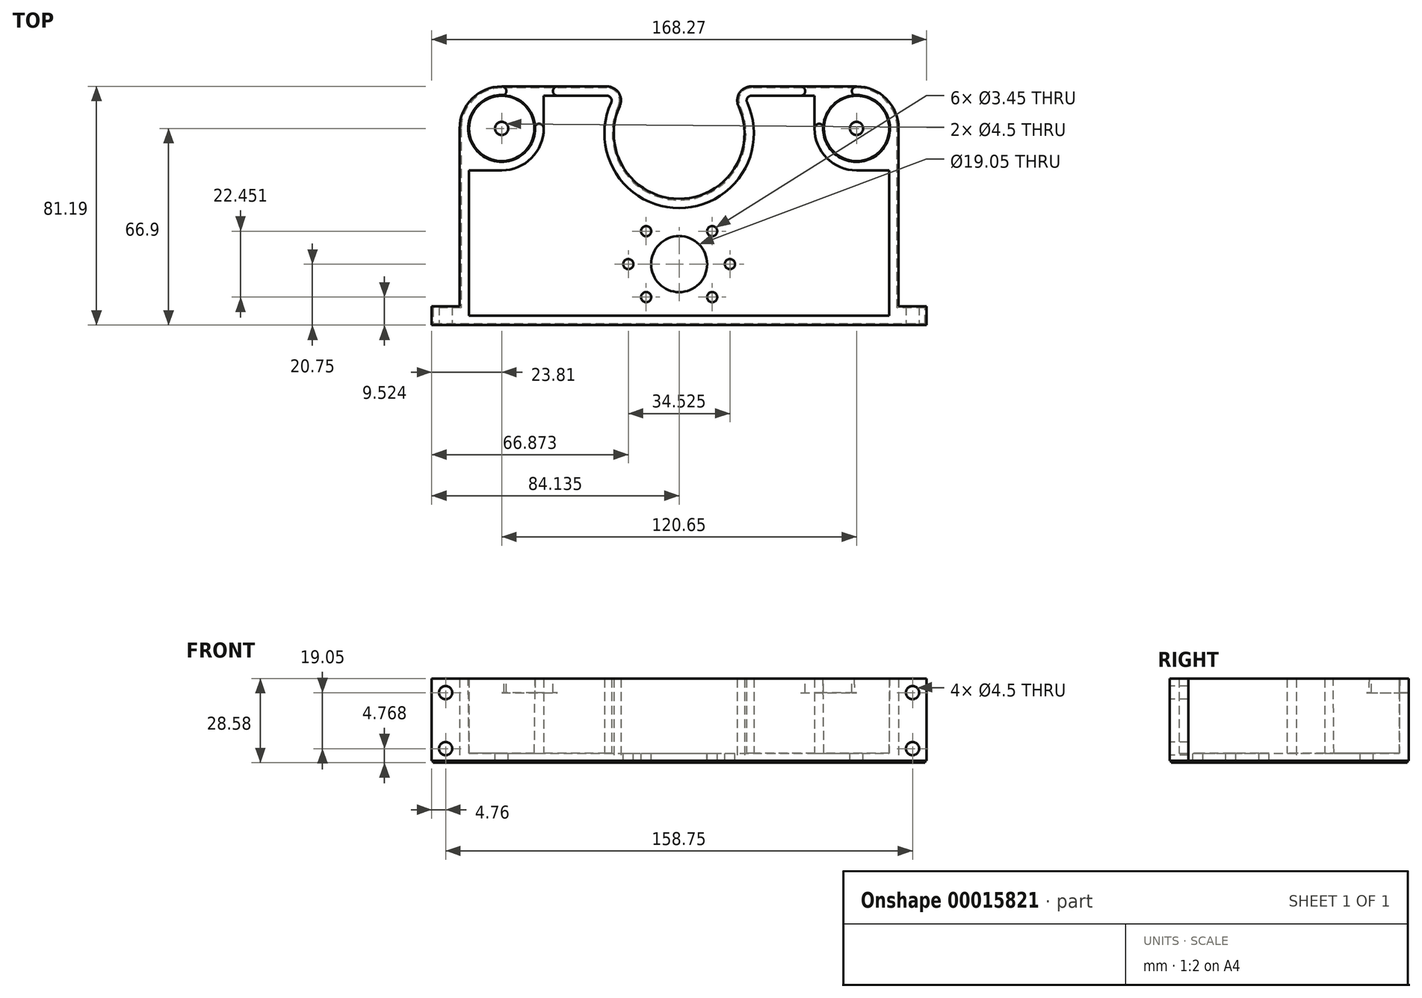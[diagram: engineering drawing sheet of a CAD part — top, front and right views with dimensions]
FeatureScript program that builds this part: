
annotation { "Feature Type Name" : "Feature", "Feature Type Description" : "" }
export const myFeature = defineFeature(function(context is Context, id is Id, definition is map)
    precondition{}
    {
        {
            var Q0;
            Q0=qCreatedBy(makeId("Top.planeOp"),FACE);
            var sketch = newSketch(context, id + "F0", { "sketchPlane" : qUnion([Q0])});
            skCircle(sketch, "E0", {"center": v(0, 0) * mm, "radius": 11.11 * mm});
            skLineSegment(sketch, "E1", {"start": v(0, 0) * mm, "end": v(120.65, 0) * mm, "construction": true});
            skCircle(sketch, "E2", {"center": v(120.65, 0) * mm, "radius": 11.11 * mm});
            skArc(sketch, "E3", {"start": v(0, 14.29) * mm, "mid": v(-10.1, 10.1) * mm, "end": v(-14.29, 0) * mm});
            skArc(sketch, "E4", {"start": v(134.94, 0) * mm, "mid": v(130.75, 10.1) * mm, "end": v(120.65, 14.29) * mm});
            skLineSegment(sketch, "E5", {"start": v(-14.29, 0) * mm, "end": v(-14.29, -60.55) * mm});
            skLineSegment(sketch, "E6", {"start": v(134.94, 0) * mm, "end": v(134.94, -60.55) * mm});
            skLineSegment(sketch, "E7", {"start": v(134.94, -60.55) * mm, "end": v(144.46, -60.55) * mm});
            skLineSegment(sketch, "E8", {"start": v(144.46, -60.55) * mm, "end": v(144.46, -66.9) * mm});
            skLineSegment(sketch, "E9", {"start": v(144.46, -66.9) * mm, "end": v(-23.81, -66.9) * mm});
            skLineSegment(sketch, "E10", {"start": v(-23.81, -66.9) * mm, "end": v(-23.81, -60.55) * mm});
            skLineSegment(sketch, "E11", {"start": v(-23.81, -60.55) * mm, "end": v(-14.29, -60.55) * mm});
            skLineSegment(sketch, "E12", {"start": v(84.87, 14.29) * mm, "end": v(35.78, 14.29) * mm, "construction": true});
            skArc(sketch, "E13", {"start": v(40.11, 7.54) * mm, "mid": v(60.32, -23.93) * mm, "end": v(80.54, 7.54) * mm});
            skLineSegment(sketch, "E14", {"start": v(60.33, -1.7) * mm, "end": v(60.33, 0) * mm, "construction": true});
            skArc(sketch, "E15", {"start": v(40.11, 7.54) * mm, "mid": v(39.8, 12.1) * mm, "end": v(35.78, 14.29) * mm});
            skLineSegment(sketch, "E16", {"start": v(0, 14.29) * mm, "end": v(35.78, 14.29) * mm});
            skArc(sketch, "E17", {"start": v(84.87, 14.29) * mm, "mid": v(80.86, 12.1) * mm, "end": v(80.54, 7.54) * mm});
            skLineSegment(sketch, "E18", {"start": v(84.87, 14.29) * mm, "end": v(120.65, 14.29) * mm});
            skLineSegment(sketch, "E19", {"start": v(60.33, -1.7) * mm, "end": v(60.33, -23.93) * mm, "construction": true});
            skLineSegment(sketch, "E20", {"start": v(60.33, -23.93) * mm, "end": v(60.33, -66.9) * mm, "construction": true});
            skSolve(sketch);
        }
        {
            var Q0;
            Q0 = qSketchRegion(id + "F0", true);
            extrude(context, id + "F1", {"entities" : qUnion([Q0]), "depth" : 25.4 * mm});
        }
        {
            var Q0;
            Q0=makeQuery(id+"F1.opExtrude","CAP_FACE",FACE,{"disambiguationData":[OSD([sQuery(id+"F0.wireOp",EDGE,"E0"),sQuery(id+"F0.wireOp",EDGE,"E2"),sQuery(id+"F0.wireOp",EDGE,"vQT7KybJ-lzgk-kh55-kQ7M-RuszsokMCCUL"),sQuery(id+"F0.wireOp",EDGE,"E3"),sQuery(id+"F0.wireOp",EDGE,"E4"),sQuery(id+"F0.wireOp",EDGE,"E5"),sQuery(id+"F0.wireOp",EDGE,"E6"),sQuery(id+"F0.wireOp",EDGE,"E7"),sQuery(id+"F0.wireOp",EDGE,"E8"),sQuery(id+"F0.wireOp",EDGE,"E9"),sQuery(id+"F0.wireOp",EDGE,"E10"),sQuery(id+"F0.wireOp",EDGE,"E11")])],"isStart":false});
            shell(context, id + "F2", {"entities" : qUnion([Q0]), "thickness" : 3.17 * mm});
        }
        {
            var Q0;
            Q0=makeQuery(id+"F2.opShell","OFFSET_FACE",FACE,{"disambiguationData":[OSD([sQuery(id+"F0.wireOp",EDGE,"E0"),sQuery(id+"F0.wireOp",EDGE,"E2"),sQuery(id+"F0.wireOp",EDGE,"vQT7KybJ-lzgk-kh55-kQ7M-RuszsokMCCUL"),sQuery(id+"F0.wireOp",EDGE,"E3"),sQuery(id+"F0.wireOp",EDGE,"E4"),sQuery(id+"F0.wireOp",EDGE,"E5"),sQuery(id+"F0.wireOp",EDGE,"E6"),sQuery(id+"F0.wireOp",EDGE,"E7"),sQuery(id+"F0.wireOp",EDGE,"E8"),sQuery(id+"F0.wireOp",EDGE,"E9"),sQuery(id+"F0.wireOp",EDGE,"E10"),sQuery(id+"F0.wireOp",EDGE,"E11")])]});
            var sketch = newSketch(context, id + "F3", { "sketchPlane" : qUnion([Q0])});
            skArc(sketch, "E21", {"start": v(14.29, 0) * mm, "mid": v(12.9, 6.16) * mm, "end": v(8.98, 11.11) * mm});
            skArc(sketch, "E22", {"start": v(-11.11, -8.98) * mm, "mid": v(-6.16, -12.9) * mm, "end": v(0, -14.29) * mm});
            skLineSegment(sketch, "E23.bottom", {"start": v(-11.11, -8.98) * mm, "end": v(0, -8.98) * mm, "construction": true});
            skLineSegment(sketch, "E23.top", {"start": v(-11.11, -14.29) * mm, "end": v(0, -14.29) * mm});
            skLineSegment(sketch, "E23.left", {"start": v(-11.11, -8.98) * mm, "end": v(-11.11, -14.29) * mm});
            skLineSegment(sketch, "E23.right", {"start": v(0, -8.98) * mm, "end": v(0, -14.29) * mm, "construction": true});
            skLineSegment(sketch, "E24.bottom", {"start": v(14.29, 0) * mm, "end": v(8.98, 0) * mm, "construction": true});
            skLineSegment(sketch, "E24.top", {"start": v(14.29, 11.11) * mm, "end": v(8.98, 11.11) * mm});
            skLineSegment(sketch, "E24.left", {"start": v(14.29, 0) * mm, "end": v(14.29, 11.11) * mm});
            skLineSegment(sketch, "E24.right", {"start": v(8.98, 0) * mm, "end": v(8.98, 11.11) * mm, "construction": true});
            skArc(sketch, "E25", {"start": v(111.67, 11.11) * mm, "mid": v(107.76, 6.16) * mm, "end": v(106.36, 0) * mm});
            skArc(sketch, "E26", {"start": v(120.65, -14.29) * mm, "mid": v(126.8, -12.9) * mm, "end": v(131.76, -8.98) * mm});
            skLineSegment(sketch, "E27.bottom", {"start": v(106.36, 0) * mm, "end": v(111.67, 0) * mm, "construction": true});
            skLineSegment(sketch, "E27.top", {"start": v(106.36, 11.11) * mm, "end": v(111.67, 11.11) * mm});
            skLineSegment(sketch, "E27.left", {"start": v(106.36, 0) * mm, "end": v(106.36, 11.11) * mm});
            skLineSegment(sketch, "E27.right", {"start": v(111.67, 0) * mm, "end": v(111.67, 11.11) * mm, "construction": true});
            skLineSegment(sketch, "E28.bottom", {"start": v(120.65, -14.29) * mm, "end": v(131.76, -14.29) * mm});
            skLineSegment(sketch, "E28.top", {"start": v(120.65, -8.98) * mm, "end": v(131.76, -8.98) * mm, "construction": true});
            skLineSegment(sketch, "E28.left", {"start": v(120.65, -14.29) * mm, "end": v(120.65, -8.98) * mm, "construction": true});
            skLineSegment(sketch, "E28.right", {"start": v(131.76, -14.29) * mm, "end": v(131.76, -8.98) * mm});
            skSolve(sketch);
        }
        {
            var Q0;
            Q0 = qSketchRegion(id + "F3", true);
            var Q1;
            Q1=makeQuery(id+"F1.opExtrude","CAP_FACE",FACE,{"disambiguationData":[OSD([sQuery(id+"F0.wireOp",EDGE,"E0"),sQuery(id+"F0.wireOp",EDGE,"E2"),sQuery(id+"F0.wireOp",EDGE,"vQT7KybJ-lzgk-kh55-kQ7M-RuszsokMCCUL"),sQuery(id+"F0.wireOp",EDGE,"E3"),sQuery(id+"F0.wireOp",EDGE,"E4"),sQuery(id+"F0.wireOp",EDGE,"E5"),sQuery(id+"F0.wireOp",EDGE,"E6"),sQuery(id+"F0.wireOp",EDGE,"E7"),sQuery(id+"F0.wireOp",EDGE,"E8"),sQuery(id+"F0.wireOp",EDGE,"E9"),sQuery(id+"F0.wireOp",EDGE,"E10"),sQuery(id+"F0.wireOp",EDGE,"E11")])],"isStart":false});
            extrude(context, id + "F4", {"entities" : qUnion([Q0]), "operationType" : NewBodyOperationType.ADD, "endBound" : BoundingType.UP_TO_SURFACE, "endBoundEntityFace" : qUnion([Q1]), "depth" : 25.4 * mm});
        }
        {
            var Q0;
            Q0=makeQuery(id+"F2.opShell","OFFSET_FACE",FACE,{"disambiguationData":[OSD([sQuery(id+"F0.wireOp",EDGE,"E0"),sQuery(id+"F0.wireOp",EDGE,"E2"),sQuery(id+"F0.wireOp",EDGE,"vQT7KybJ-lzgk-kh55-kQ7M-RuszsokMCCUL"),sQuery(id+"F0.wireOp",EDGE,"E3"),sQuery(id+"F0.wireOp",EDGE,"E4"),sQuery(id+"F0.wireOp",EDGE,"E5"),sQuery(id+"F0.wireOp",EDGE,"E6"),sQuery(id+"F0.wireOp",EDGE,"E7"),sQuery(id+"F0.wireOp",EDGE,"E8"),sQuery(id+"F0.wireOp",EDGE,"E9"),sQuery(id+"F0.wireOp",EDGE,"E10"),sQuery(id+"F0.wireOp",EDGE,"E11")])]});
            var Q1;
            Q1=makeQuery(id+"F1.opExtrude","CAP_FACE",FACE,{"disambiguationData":[OSD([sQuery(id+"F0.wireOp",EDGE,"E0"),sQuery(id+"F0.wireOp",EDGE,"E2"),sQuery(id+"F0.wireOp",EDGE,"vQT7KybJ-lzgk-kh55-kQ7M-RuszsokMCCUL"),sQuery(id+"F0.wireOp",EDGE,"E3"),sQuery(id+"F0.wireOp",EDGE,"E4"),sQuery(id+"F0.wireOp",EDGE,"E5"),sQuery(id+"F0.wireOp",EDGE,"E6"),sQuery(id+"F0.wireOp",EDGE,"E7"),sQuery(id+"F0.wireOp",EDGE,"E8"),sQuery(id+"F0.wireOp",EDGE,"E9"),sQuery(id+"F0.wireOp",EDGE,"E10"),sQuery(id+"F0.wireOp",EDGE,"E11")])],"isStart":true});
            extrude(context, id + "F5", {"entities" : qUnion([Q0]), "operationType" : NewBodyOperationType.REMOVE, "endBound" : BoundingType.UP_TO_SURFACE, "oppositeDirection" : true, "endBoundEntityFace" : qUnion([Q1]), "depth" : 25.4 * mm});
        }
        {
            var Q0;
            Q0=makeQuery(id+"F1.opExtrude","CAP_FACE",FACE,{"disambiguationData":[OSD([sQuery(id+"F0.wireOp",EDGE,"E0"),sQuery(id+"F0.wireOp",EDGE,"E2"),sQuery(id+"F0.wireOp",EDGE,"vQT7KybJ-lzgk-kh55-kQ7M-RuszsokMCCUL"),sQuery(id+"F0.wireOp",EDGE,"E3"),sQuery(id+"F0.wireOp",EDGE,"E4"),sQuery(id+"F0.wireOp",EDGE,"E5"),sQuery(id+"F0.wireOp",EDGE,"E6"),sQuery(id+"F0.wireOp",EDGE,"E7"),sQuery(id+"F0.wireOp",EDGE,"E8"),sQuery(id+"F0.wireOp",EDGE,"E9"),sQuery(id+"F0.wireOp",EDGE,"E10"),sQuery(id+"F0.wireOp",EDGE,"E11")])],"isStart":true});
            var sketch = newSketch(context, id + "F6", { "sketchPlane" : qUnion([Q0])});
            skCircle(sketch, "E29", {"center": v(120.65, 0) * mm, "radius": 2.25 * mm});
            skCircle(sketch, "E30", {"center": v(0, 0) * mm, "radius": 2.25 * mm});
            skLineSegment(sketch, "E31", {"start": v(120.65, 0) * mm, "end": v(0, 0) * mm, "construction": true});
            skLineSegment(sketch, "E32.bottom", {"start": v(49.1, 34.92) * mm, "end": v(71.55, 34.92) * mm, "construction": true});
            skLineSegment(sketch, "E32.top", {"start": v(49.1, 57.38) * mm, "end": v(71.55, 57.38) * mm, "construction": true});
            skLineSegment(sketch, "E32.left", {"start": v(49.1, 34.92) * mm, "end": v(49.1, 57.38) * mm, "construction": true});
            skLineSegment(sketch, "E32.right", {"start": v(71.55, 34.92) * mm, "end": v(71.55, 57.38) * mm, "construction": true});
            skPoint(sketch, "E32.middle", {"position": v(60.33, 46.15) * mm});
            skCircle(sketch, "E33", {"center": v(60.33, 46.15) * mm, "radius": 11.11 * mm, "construction": true});
            skCircle(sketch, "E34", {"center": v(49.1, 34.92) * mm, "radius": 4.76 * mm, "construction": true});
            skCircle(sketch, "E35", {"center": v(71.55, 34.92) * mm, "radius": 1.73 * mm});
            skCircle(sketch, "E36", {"center": v(49.1, 34.92) * mm, "radius": 1.73 * mm});
            skCircle(sketch, "E37", {"center": v(49.1, 57.38) * mm, "radius": 1.73 * mm});
            skCircle(sketch, "E38", {"center": v(71.55, 57.38) * mm, "radius": 1.73 * mm});
            skCircle(sketch, "E39", {"center": v(60.33, 46.15) * mm, "radius": 9.53 * mm});
            skLineSegment(sketch, "E40", {"start": v(60.32, 46.15) * mm, "end": v(60.33, 0) * mm, "construction": true});
            skLineSegment(sketch, "E41", {"start": v(77.59, 46.15) * mm, "end": v(43.06, 46.15) * mm, "construction": true});
            skCircle(sketch, "E42", {"center": v(77.59, 46.15) * mm, "radius": 1.73 * mm});
            skCircle(sketch, "E43", {"center": v(43.06, 46.15) * mm, "radius": 1.73 * mm});
            skSolve(sketch);
        }
        {
            var Q0;
            {var subQ13=sQuery(id+"F0.wireOp",EDGE,"E0");var subQ16=makeQuery(id+"F1.opExtrude","CAP_EDGE",EDGE,{"disambiguationData":[OSD([subQ13])],"isStart":true});Q0=makeQuery(id+"F6.imprint","IMPRINT",FACE,{"disambiguationData":[TD([[makeQuery(id+"F6.imprint","IMPRINT",EDGE,{"derivedFrom":subQ16}),1.0]])]});}
            var Q1;
            Q1=makeQuery(id+"F6.imprint","IMPRINT",FACE,{"disambiguationData":[TD([[makeQuery(id+"F6.imprint","IMPRINT",EDGE,{"derivedFrom":sQuery(id+"F6.wireOp",EDGE,"E35")}),-1.0]])]});
            var Q2;
            Q2=makeQuery(id+"F6.imprint","IMPRINT",FACE,{"disambiguationData":[TD([[makeQuery(id+"F6.imprint","IMPRINT",EDGE,{"derivedFrom":sQuery(id+"F6.wireOp",EDGE,"E30")}),-1.0]])]});
            var Q3;
            Q3=makeQuery(id+"F6.imprint","IMPRINT",FACE,{"disambiguationData":[TD([[makeQuery(id+"F6.imprint","IMPRINT",EDGE,{"derivedFrom":sQuery(id+"F6.wireOp",EDGE,"E29")}),-1.0]])]});
            extrude(context, id + "F7", {"entities" : qUnion([Q0, Q1, Q2, Q3]), "operationType" : NewBodyOperationType.ADD, "depth" : 3.17 * mm});
        }
        {
            var Q0;
            {var subQ0=sQuery(id+"F0.wireOp",EDGE,"E9");Q0=makeQuery(id+"F7.boolean.opBoolean","MERGE",FACE,{"derivedFrom":[makeQuery(id+"F1.opExtrude","SWEPT_FACE",FACE,{"disambiguationData":[OSD([subQ0])]}),makeQuery(id+"F7.opExtrude","SWEPT_FACE",FACE,{"disambiguationData":[OSD([subQ0])]})]});}
            var sketch = newSketch(context, id + "F8", { "sketchPlane" : qUnion([Q0])});
            skLineSegment(sketch, "E44.bottom", {"start": v(-19.05, 25.4) * mm, "end": v(-23.81, 25.4) * mm, "construction": true});
            skLineSegment(sketch, "E44.top", {"start": v(-19.05, 20.64) * mm, "end": v(-23.81, 20.64) * mm, "construction": true});
            skLineSegment(sketch, "E44.left", {"start": v(-19.05, 25.4) * mm, "end": v(-19.05, 20.64) * mm, "construction": true});
            skLineSegment(sketch, "E44.right", {"start": v(-23.81, 25.4) * mm, "end": v(-23.81, 20.64) * mm, "construction": true});
            skLineSegment(sketch, "E45", {"start": v(60.33, 25.4) * mm, "end": v(60.33, -3.18) * mm, "construction": true});
            skLineSegment(sketch, "E46.bottom", {"start": v(-19.05, 20.64) * mm, "end": v(139.7, 20.64) * mm, "construction": true});
            skLineSegment(sketch, "E46.top", {"start": v(-19.05, 1.59) * mm, "end": v(139.7, 1.59) * mm, "construction": true});
            skLineSegment(sketch, "E46.left", {"start": v(-19.05, 20.64) * mm, "end": v(-19.05, 1.59) * mm, "construction": true});
            skLineSegment(sketch, "E46.right", {"start": v(139.7, 20.64) * mm, "end": v(139.7, 1.59) * mm, "construction": true});
            skPoint(sketch, "E46.middle", {"position": v(60.33, 11.11) * mm});
            skCircle(sketch, "E47", {"center": v(-19.05, 20.64) * mm, "radius": 2.25 * mm});
            skCircle(sketch, "E48", {"center": v(-19.05, 1.59) * mm, "radius": 2.25 * mm});
            skCircle(sketch, "E49", {"center": v(139.7, 1.59) * mm, "radius": 2.25 * mm});
            skCircle(sketch, "E50", {"center": v(139.7, 20.64) * mm, "radius": 2.25 * mm});
            skSolve(sketch);
        }
        {
            var Q0;
            Q0 = qSketchRegion(id + "F8", true);
            var Q1;
            {var subQ0=sQuery(id+"F0.wireOp",EDGE,"E7");Q1=makeQuery(id+"F7.boolean.opBoolean","MERGE",FACE,{"derivedFrom":[makeQuery(id+"F1.opExtrude","SWEPT_FACE",FACE,{"disambiguationData":[OSD([subQ0])]}),makeQuery(id+"F7.opExtrude","SWEPT_FACE",FACE,{"disambiguationData":[OSD([subQ0])]})]});}
            extrude(context, id + "F9", {"entities" : qUnion([Q0]), "operationType" : NewBodyOperationType.REMOVE, "endBound" : BoundingType.UP_TO_SURFACE, "oppositeDirection" : true, "endBoundEntityFace" : qUnion([Q1]), "depth" : 25.4 * mm});
        }
        {
            var Q0;
            Q0=makeQuery(id+"F1.opExtrude","CAP_EDGE",EDGE,{"disambiguationData":[OSD([sQuery(id+"F0.wireOp",EDGE,"E2")])],"isStart":false});
            var Q1;
            Q1=makeQuery(id+"F1.opExtrude","CAP_EDGE",EDGE,{"disambiguationData":[OSD([sQuery(id+"F0.wireOp",EDGE,"E0")])],"isStart":false});
            chamfer(context, id + "F10", {"entities" : qUnion([Q0, Q1]), "chamferType" : ChamferType.TWO_OFFSETS, "width1" : 25.4 * mm, "oppositeDirection" : false, "width2" : 0.25 * mm, "tangentPropagation" : true});
        }
        {
            var Q0;
            {var subQ0=sQuery(id+"F0.wireOp",EDGE,"E18");var subQ1=sQuery(id+"F0.wireOp",EDGE,"E17");var subQ2=sQuery(id+"F0.wireOp",EDGE,"E16");var subQ3=sQuery(id+"F0.wireOp",EDGE,"E15");var subQ4=sQuery(id+"F0.wireOp",EDGE,"E13");var subQ5=sQuery(id+"F0.wireOp",EDGE,"E11");var subQ6=sQuery(id+"F0.wireOp",EDGE,"E10");var subQ7=sQuery(id+"F0.wireOp",EDGE,"E9");var subQ8=sQuery(id+"F0.wireOp",EDGE,"E8");var subQ9=sQuery(id+"F0.wireOp",EDGE,"E7");var subQ10=sQuery(id+"F0.wireOp",EDGE,"E6");var subQ11=sQuery(id+"F0.wireOp",EDGE,"E5");var subQ12=sQuery(id+"F0.wireOp",EDGE,"E4");var subQ13=sQuery(id+"F0.wireOp",EDGE,"E3");var subQ14=sQuery(id+"F0.wireOp",EDGE,"E2");var subQ15=sQuery(id+"F0.wireOp",EDGE,"E0");Q0=makeQuery(id+"F4.boolean.opBoolean","MERGE",FACE,{"derivedFrom":[makeQuery(id+"F1.opExtrude","CAP_FACE",FACE,{"disambiguationData":[OSD([subQ15,subQ14,subQ13,subQ12,subQ11,subQ10,subQ9,subQ8,subQ7,subQ6,subQ5,subQ4,subQ3,subQ2,subQ1,subQ0])],"isStart":false}),makeQuery(id+"F4.opExtrude","CAP_FACE",FACE,{"disambiguationData":[OSD([subQ15,subQ14,subQ13,subQ12,subQ11,subQ10,subQ9,subQ8,subQ7,subQ6,subQ5,subQ4,subQ3,subQ2,subQ1,subQ0]),ownerDisambiguation([makeQuery(id+"F4.opExtrude","SWEPT_BODY",BODY,{"disambiguationData":[OSD([sQuery(id+"F3.wireOp",EDGE,"E21"),sQuery(id+"F3.wireOp",EDGE,"E24.top"),sQuery(id+"F3.wireOp",EDGE,"E24.left")])]})])],"isStart":false}),makeQuery(id+"F4.opExtrude","CAP_FACE",FACE,{"disambiguationData":[OSD([subQ15,subQ14,subQ13,subQ12,subQ11,subQ10,subQ9,subQ8,subQ7,subQ6,subQ5,subQ4,subQ3,subQ2,subQ1,subQ0]),ownerDisambiguation([makeQuery(id+"F4.opExtrude","SWEPT_BODY",BODY,{"disambiguationData":[OSD([sQuery(id+"F3.wireOp",EDGE,"E22"),sQuery(id+"F3.wireOp",EDGE,"E23.top"),sQuery(id+"F3.wireOp",EDGE,"E23.left")])]})])],"isStart":false}),makeQuery(id+"F4.opExtrude","CAP_FACE",FACE,{"disambiguationData":[OSD([subQ15,subQ14,subQ13,subQ12,subQ11,subQ10,subQ9,subQ8,subQ7,subQ6,subQ5,subQ4,subQ3,subQ2,subQ1,subQ0]),ownerDisambiguation([makeQuery(id+"F4.opExtrude","SWEPT_BODY",BODY,{"disambiguationData":[OSD([sQuery(id+"F3.wireOp",EDGE,"E25"),sQuery(id+"F3.wireOp",EDGE,"E27.top"),sQuery(id+"F3.wireOp",EDGE,"E27.left")])]})])],"isStart":false}),makeQuery(id+"F4.opExtrude","CAP_FACE",FACE,{"disambiguationData":[OSD([subQ15,subQ14,subQ13,subQ12,subQ11,subQ10,subQ9,subQ8,subQ7,subQ6,subQ5,subQ4,subQ3,subQ2,subQ1,subQ0]),ownerDisambiguation([makeQuery(id+"F4.opExtrude","SWEPT_BODY",BODY,{"disambiguationData":[OSD([sQuery(id+"F3.wireOp",EDGE,"E26"),sQuery(id+"F3.wireOp",EDGE,"E28.bottom"),sQuery(id+"F3.wireOp",EDGE,"E28.right")])]})])],"isStart":false})]});}
            var sketch = newSketch(context, id + "F11", { "sketchPlane" : qUnion([Q0])});
            skArc(sketch, "E51", {"start": v(0, 11.11) * mm, "mid": v(1.59, 12.7) * mm, "end": v(0, 14.29) * mm});
            skArc(sketch, "E52", {"start": v(14.29, 0) * mm, "mid": v(12.7, 1.59) * mm, "end": v(11.11, 0) * mm});
            skArc(sketch, "E53", {"start": v(19.01, 14.29) * mm, "mid": v(17.43, 12.7) * mm, "end": v(19.01, 11.11) * mm});
            skArc(sketch, "E54", {"start": v(11.11, 0) * mm, "mid": v(7.86, 7.86) * mm, "end": v(0, 11.11) * mm});
            skLineSegment(sketch, "E55", {"start": v(0, 14.29) * mm, "end": v(19.01, 14.29) * mm});
            skLineSegment(sketch, "E56", {"start": v(19.01, 11.11) * mm, "end": v(14.29, 11.11) * mm});
            skLineSegment(sketch, "E57", {"start": v(14.29, 11.11) * mm, "end": v(14.29, 0) * mm});
            skArc(sketch, "E58", {"start": v(109.54, 0) * mm, "mid": v(107.95, 1.59) * mm, "end": v(106.36, 0) * mm});
            skArc(sketch, "E59", {"start": v(120.65, 14.29) * mm, "mid": v(119.06, 12.7) * mm, "end": v(120.65, 11.11) * mm});
            skArc(sketch, "E60", {"start": v(101.64, 11.11) * mm, "mid": v(103.22, 12.7) * mm, "end": v(101.64, 14.29) * mm});
            skLineSegment(sketch, "E61", {"start": v(101.64, 11.11) * mm, "end": v(106.36, 11.11) * mm});
            skLineSegment(sketch, "E62", {"start": v(106.36, 11.11) * mm, "end": v(106.36, 0) * mm});
            skLineSegment(sketch, "E63", {"start": v(101.64, 14.29) * mm, "end": v(120.65, 14.29) * mm});
            skArc(sketch, "E64", {"start": v(120.65, 11.11) * mm, "mid": v(112.8, 7.86) * mm, "end": v(109.54, 0) * mm});
            skSolve(sketch);
        }
        {
            var Q0;
            Q0 = qSketchRegion(id + "F11", true);
            extrude(context, id + "F12", {"entities" : qUnion([Q0]), "operationType" : NewBodyOperationType.REMOVE, "oppositeDirection" : true, "depth" : 4.76 * mm});
        }
        {
            var Q0;
            {var subQ0=sQuery(id+"F0.wireOp",EDGE,"E10");Q0=makeQuery(id+"F7.boolean.opBoolean","MERGE",FACE,{"derivedFrom":[makeQuery(id+"F1.opExtrude","SWEPT_FACE",FACE,{"disambiguationData":[OSD([subQ0])]}),makeQuery(id+"F7.opExtrude","SWEPT_FACE",FACE,{"disambiguationData":[OSD([subQ0])]})]});}
            var sketch = newSketch(context, id + "F13", { "sketchPlane" : qUnion([Q0])});
            skLineSegment(sketch, "E65.bottom", {"start": v(66.9, -3.18) * mm, "end": v(66.4, -3.18) * mm});
            skLineSegment(sketch, "E65.top", {"start": v(66.9, -2.54) * mm, "end": v(66.4, -2.54) * mm});
            skLineSegment(sketch, "E65.left", {"start": v(66.9, -3.18) * mm, "end": v(66.9, -2.54) * mm});
            skLineSegment(sketch, "E65.right", {"start": v(66.4, -3.18) * mm, "end": v(66.4, -2.54) * mm});
            skSolve(sketch);
        }
        {
            var Q0;
            Q0=makeQuery(id+"F13.imprint","IMPRINT",FACE,{"disambiguationData":[TD([[makeQuery(id+"F13.imprint","IMPRINT",EDGE,{"derivedFrom":sQuery(id+"F13.wireOp",EDGE,"E65.bottom")}),-1.0]])]});
            var Q1;
            Q1=makeQuery(id+"F7.opExtrude","CAP_EDGE",EDGE,{"disambiguationData":[OSD([sQuery(id+"F0.wireOp",EDGE,"E9")])],"isStart":false});
            var Q2;
            Q2=makeQuery(id+"F7.opExtrude","CAP_EDGE",EDGE,{"disambiguationData":[OSD([sQuery(id+"F0.wireOp",EDGE,"E8")])],"isStart":false});
            var Q3;
            Q3=makeQuery(id+"F7.opExtrude","CAP_EDGE",EDGE,{"disambiguationData":[OSD([sQuery(id+"F0.wireOp",EDGE,"E7")])],"isStart":false});
            var Q4;
            Q4=makeQuery(id+"F7.opExtrude","CAP_EDGE",EDGE,{"disambiguationData":[OSD([sQuery(id+"F0.wireOp",EDGE,"E6")])],"isStart":false});
            var Q5;
            Q5=makeQuery(id+"F7.opExtrude","CAP_EDGE",EDGE,{"disambiguationData":[OSD([sQuery(id+"F0.wireOp",EDGE,"E4")])],"isStart":false});
            var Q6;
            Q6=makeQuery(id+"F7.opExtrude","CAP_EDGE",EDGE,{"disambiguationData":[OSD([sQuery(id+"F0.wireOp",EDGE,"E18")])],"isStart":false});
            var Q7;
            Q7=makeQuery(id+"F7.opExtrude","CAP_EDGE",EDGE,{"disambiguationData":[OSD([sQuery(id+"F0.wireOp",EDGE,"E17")])],"isStart":false});
            var Q8;
            Q8=makeQuery(id+"F7.opExtrude","CAP_EDGE",EDGE,{"disambiguationData":[OSD([sQuery(id+"F0.wireOp",EDGE,"E13")])],"isStart":false});
            var Q9;
            Q9=makeQuery(id+"F7.opExtrude","CAP_EDGE",EDGE,{"disambiguationData":[OSD([sQuery(id+"F0.wireOp",EDGE,"E15")])],"isStart":false});
            var Q10;
            Q10=makeQuery(id+"F7.opExtrude","CAP_EDGE",EDGE,{"disambiguationData":[OSD([sQuery(id+"F0.wireOp",EDGE,"E16")])],"isStart":false});
            var Q11;
            Q11=makeQuery(id+"F7.opExtrude","CAP_EDGE",EDGE,{"disambiguationData":[OSD([sQuery(id+"F0.wireOp",EDGE,"E3")])],"isStart":false});
            var Q12;
            Q12=makeQuery(id+"F7.opExtrude","CAP_EDGE",EDGE,{"disambiguationData":[OSD([sQuery(id+"F0.wireOp",EDGE,"E5")])],"isStart":false});
            var Q13;
            Q13=makeQuery(id+"F7.opExtrude","CAP_EDGE",EDGE,{"disambiguationData":[OSD([sQuery(id+"F0.wireOp",EDGE,"E11")])],"isStart":false});
            var Q14;
            Q14=makeQuery(id+"F7.opExtrude","CAP_EDGE",EDGE,{"disambiguationData":[OSD([sQuery(id+"F0.wireOp",EDGE,"E10")])],"isStart":false});
            sweep(context, id + "F14", {"operationType" : NewBodyOperationType.REMOVE, "profiles" : qUnion([Q0]), "path" : qUnion([Q1, Q2, Q3, Q4, Q5, Q6, Q7, Q8, Q9, Q10, Q11, Q12, Q13, Q14])});
        }
    });
